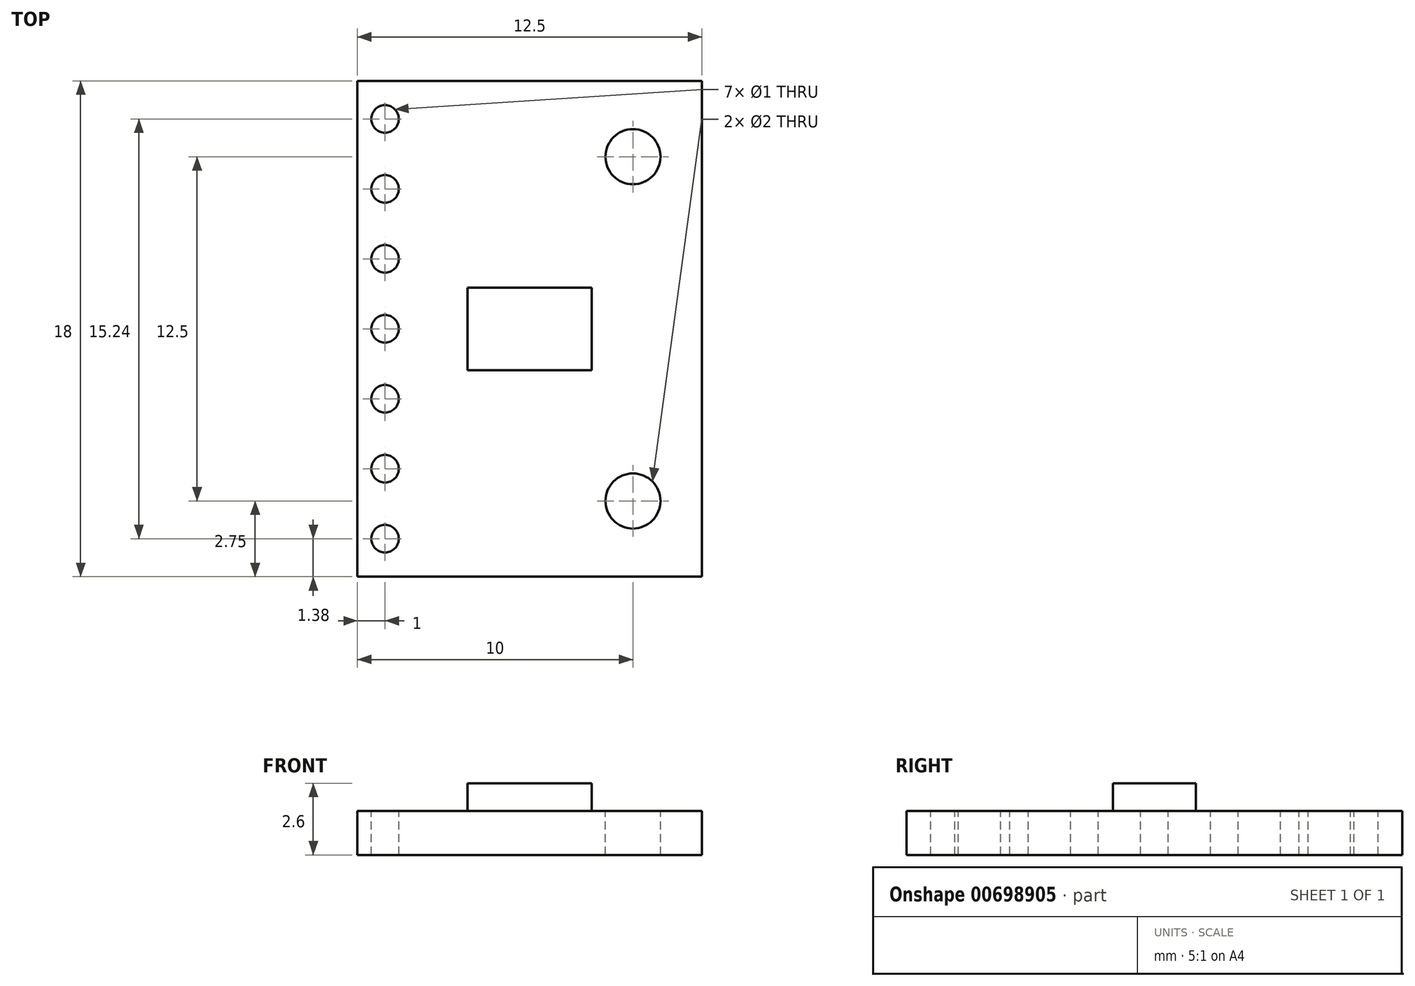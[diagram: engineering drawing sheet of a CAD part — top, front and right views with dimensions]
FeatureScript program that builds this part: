
annotation { "Feature Type Name" : "Feature", "Feature Type Description" : "" }
export const myFeature = defineFeature(function(context is Context, id is Id, definition is map)
    precondition{}
    {
        {
            var Q0;
            Q0=qCreatedBy(makeId("Top.planeOp"),FACE);
            var sketch = newSketch(context, id + "F0", { "sketchPlane" : qUnion([Q0])});
            skLineSegment(sketch, "E0.bottom", {"start": v(6.25, 9) * mm, "end": v(-6.25, 9) * mm});
            skLineSegment(sketch, "E0.top", {"start": v(6.25, -9) * mm, "end": v(-6.25, -9) * mm});
            skLineSegment(sketch, "E0.left", {"start": v(6.25, 9) * mm, "end": v(6.25, -9) * mm});
            skLineSegment(sketch, "E0.right", {"start": v(-6.25, 9) * mm, "end": v(-6.25, -9) * mm});
            skPoint(sketch, "E0.middle", {"position": v(0, 0) * mm});
            skCircle(sketch, "E1", {"center": v(3.75, 6.25) * mm, "radius": 1 * mm});
            skCircle(sketch, "E2", {"center": v(3.75, -6.25) * mm, "radius": 1 * mm});
            skLineSegment(sketch, "E3", {"start": v(3.75, 6.25) * mm, "end": v(3.75, -6.25) * mm, "construction": true});
            skLineSegment(sketch, "E4", {"start": v(0, 0) * mm, "end": v(3.75, 0) * mm, "construction": true});
            skLineSegment(sketch, "E5.bottom", {"start": v(2.25, 1.5) * mm, "end": v(-2.25, 1.5) * mm});
            skLineSegment(sketch, "E5.top", {"start": v(2.25, -1.5) * mm, "end": v(-2.25, -1.5) * mm});
            skLineSegment(sketch, "E5.left", {"start": v(2.25, 1.5) * mm, "end": v(2.25, -1.5) * mm});
            skLineSegment(sketch, "E5.right", {"start": v(-2.25, 1.5) * mm, "end": v(-2.25, -1.5) * mm});
            skCircle(sketch, "E6", {"center": v(-5.25, 7.62) * mm, "radius": 0.5 * mm});
            skCircle(sketch, "E7.1.0.0", {"center": v(-5.25, 5.08) * mm, "radius": 0.5 * mm});
            skCircle(sketch, "E7.2.0.0", {"center": v(-5.25, 2.54) * mm, "radius": 0.5 * mm});
            skCircle(sketch, "E7.3.0.0", {"center": v(-5.25, 0) * mm, "radius": 0.5 * mm});
            skCircle(sketch, "E7.4.0.0", {"center": v(-5.25, -2.54) * mm, "radius": 0.5 * mm});
            skCircle(sketch, "E7.5.0.0", {"center": v(-5.25, -5.08) * mm, "radius": 0.5 * mm});
            skCircle(sketch, "E7.6.0.0", {"center": v(-5.25, -7.62) * mm, "radius": 0.5 * mm});
            skLineSegment(sketch, "E7.direction1", {"start": v(-5.25, 7.62) * mm, "end": v(-5.25, 5.08) * mm, "construction": true});
            skSolve(sketch);
        }
        {
            var Q0;
            Q0=makeQuery(id+"F0.imprint","IMPRINT",FACE,{"disambiguationData":[TD([[makeQuery(id+"F0.imprint","IMPRINT",EDGE,{"derivedFrom":sQuery(id+"F0.wireOp",EDGE,"E0.bottom")}),1.0]])]});
            var Q1;
            Q1=makeQuery(id+"F0.imprint","IMPRINT",FACE,{"disambiguationData":[TD([[makeQuery(id+"F0.imprint","IMPRINT",EDGE,{"derivedFrom":sQuery(id+"F0.wireOp",EDGE,"E5.bottom")}),1.0]])]});
            extrude(context, id + "F1", {"entities" : qUnion([Q0, Q1]), "oppositeDirection" : true, "depth" : 1.6 * mm});
        }
        {
            var Q0;
            Q0=makeQuery(id+"F0.imprint","IMPRINT",FACE,{"disambiguationData":[TD([[makeQuery(id+"F0.imprint","IMPRINT",EDGE,{"derivedFrom":sQuery(id+"F0.wireOp",EDGE,"E5.bottom")}),1.0]])]});
            extrude(context, id + "F2", {"entities" : qUnion([Q0]), "operationType" : NewBodyOperationType.ADD, "depth" : 1 * mm});
        }
    });
